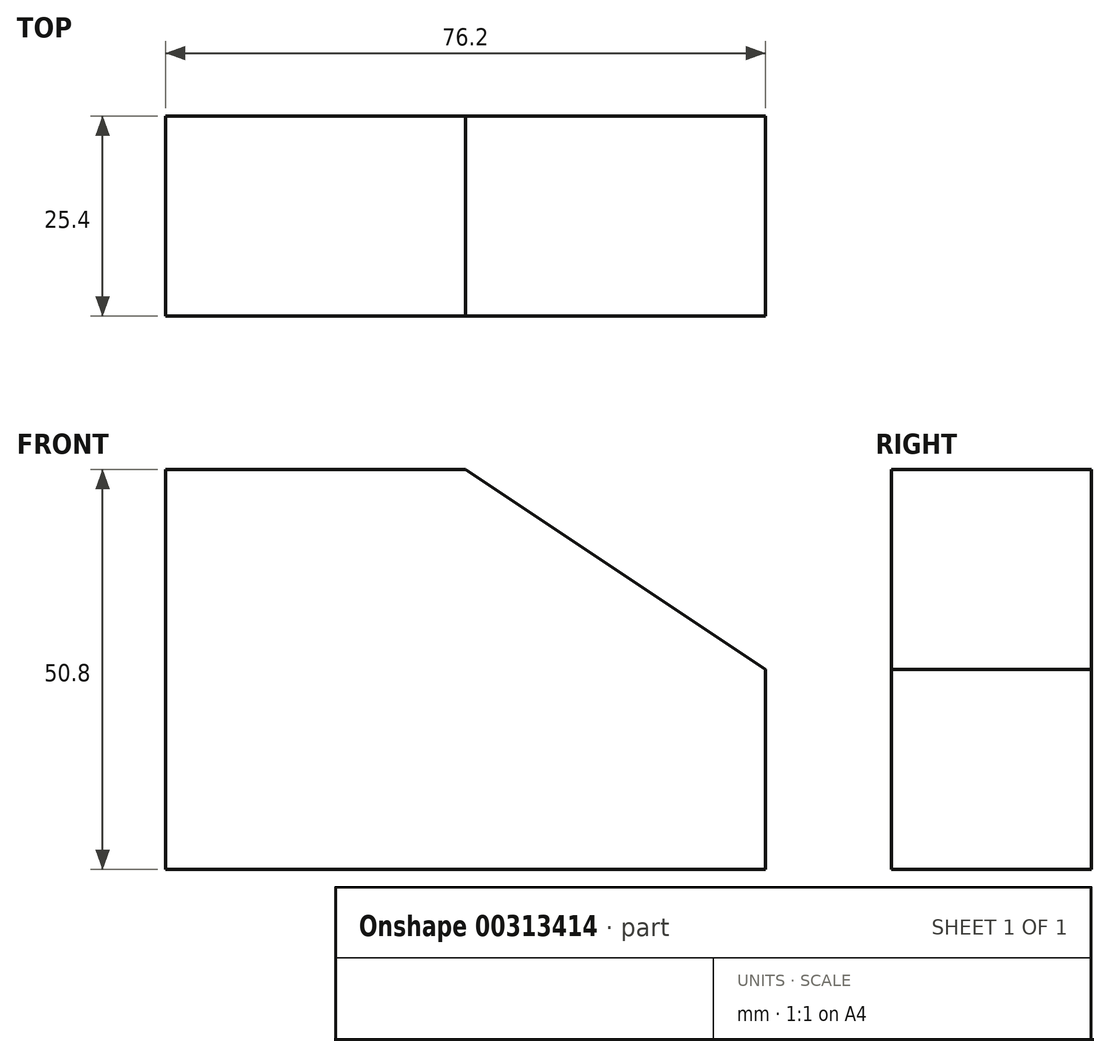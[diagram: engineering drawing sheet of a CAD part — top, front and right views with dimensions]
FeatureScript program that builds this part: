
annotation { "Feature Type Name" : "Feature", "Feature Type Description" : "" }
export const myFeature = defineFeature(function(context is Context, id is Id, definition is map)
    precondition{}
    {
        {
            var Q0;
            Q0=qCreatedBy(makeId("Front.planeOp"),FACE);
            var sketch = newSketch(context, id + "F0", { "sketchPlane" : qUnion([Q0])});
            skLineSegment(sketch, "E0", {"start": v(-38.1, -53.68) * mm, "end": v(38.1, -53.68) * mm});
            skLineSegment(sketch, "E1", {"start": v(38.1, -53.68) * mm, "end": v(38.1, -28.28) * mm});
            skLineSegment(sketch, "E2", {"start": v(-38.1, -53.68) * mm, "end": v(-38.1, -2.88) * mm});
            skLineSegment(sketch, "E3", {"start": v(-38.1, -2.88) * mm, "end": v(0, -2.88) * mm});
            skLineSegment(sketch, "E4", {"start": v(0, -2.88) * mm, "end": v(38.1, -28.28) * mm});
            skSolve(sketch);
        }
        {
            var Q0;
            Q0=makeQuery(id+"F0.imprint","IMPRINT",FACE,{"disambiguationData":[TD([[makeQuery(id+"F0.imprint","IMPRINT",EDGE,{"derivedFrom":sQuery(id+"F0.wireOp",EDGE,"E0")}),1.0]])]});
            extrude(context, id + "F1", {"entities" : qUnion([Q0]), "depth" : 25.4 * mm});
        }
    });
